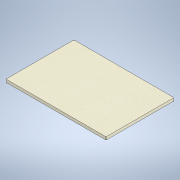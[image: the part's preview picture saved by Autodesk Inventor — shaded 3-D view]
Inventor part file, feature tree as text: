
AUTODESK INVENTOR PART (.ipt)
format: ipt  version: 2021 (Build 250183000, 183)  size: 114,688 bytes
history: native  units: mm
features: extrude x1, sketch x1
ambient origin geometry x8: Origin, YZ Plane, XZ Plane, XY Plane, X Axis, Y Axis, Z Axis, Center Point
bodies: Solid1 (feature_tree)
feature tree (2):
  extrude  "Extrusion1"  Depth=190.0mm
  sketch  "Sketch1"  dims[d0=280.0mm d1=190.0mm d2=2.0mm d3=8.0mm d4=0.0mm]
